# Revit family: KS ALU-PU 80, DS 20, M10-M12, Ø168,3 mit Blechz.
name_source: partatom
category: HLS-Bauteile
revit_build: Autodesk Revit 2018 (Build: 20190510_1515(x64)
units: mm (PartAtom-declared; Revit-internal decimal feet)

## family parameters
Arbeitsebenenbasiert = Ja
Beim Laden mit Abzugskörper schneiden = Nein
Bemaßung runder Anschluss = Durchmesser verwenden
Gemeinsam genutzt = Ja
Immer vertikal = Nein
Raumberechnungspunkt = Nein
Teiletyp = Normal

## types (1)
- Kälteschelle ALU-PU 80, DS 20, M10/M12, Ø168,3
    A = 46 mm  [stored 0.150919 ft]
    AB = 1 mm  [stored 0.00328084 ft]
    Anschluss = M10/M12
    Anschlußhöhe = 47 mm
    Artikelnummer = 75616844/B
    B = 288 mm  [stored 0.944882 ft]
    Baustoffklasse = B2
    Breite = 287 mm  [stored 0.941601 ft]
    D = 168 mm
    D0 = 208 mm
    DF1 = 34 mm
    DF2 = 34 mm
    DS = 20 mm  [stored 0.0656168 ft]
    DVS = 18 mm  [stored 0.0590551 ft]
    Dichte Kern = 80 kg/m³
    Dichte Mantel = 2700 kg/m³
    Dicke Mantel = 0.08 mm
    Dmax = 172 mm  [stored 0.564304 ft]
    Dmin = 167 mm  [stored 0.5479 ft]
    Druckverteilung = Bechzylinder
    Dämmkörper = ALU/PU
    Dämmstärke = 20 mm  [stored 0.0656168 ft]
    EAN = 4250928443793
    Fabrikat = MEFA
    Firma = MEFA Befestigungs- und Montagesysteme GmbH
    Gewicht = 1.41 kg
    Gewicht pro Bauteil = 1.41 kg
    H = 238 mm
    HGA = 22 mm  [stored 0.0721785 ft]
    Kurztext1 = Kälteschelle RG80 ALU/PU
    Kurztext2 = 168,3 mm Iso 20 x 100 mm M10/M12
    L = 100 mm  [stored 0.328084 ft]
    MB = 35 mm  [stored 0.114829 ft]
    MD = 4 mm  [stored 0.0131234 ft]
    Material = Stahl
    Material Mantel = Alufolie
    Materialname = S235
    Mengeneinheit = St
    Oberflaeche = galvanisch verzinkt
    R = 104 mm
    RM = 108 mm
    Rohraußendurchmesser Stahl = 168,3 mm
    Rohrschellentyp = Maxima PSM
    S = 254 mm  [stored 0.833333 ft]
    Schalenlänge = 100 mm
    Vorgabe-Ansicht = 1219 mm
    Wasserdampfdiffusionswiderstand = 18750 µ
    Wärmeleitfähigkeit = 0.025 W/mK
    max. Temperaturbeständigkeit = 120 °C
    max. zul. Last = 2.50 kN
    mittl. Nenndruckfestigkeit Kern = 0,5 N/mm²
    stat. Belastung Kern = 0.10 N/mm²
    vpe = 1

note: [stored X ft] marks values corroborated as IEEE doubles in the binary element streams (Revit-internal decimal feet)

## geometry (parser evidence)
native form markers: Sweep x2
no freeform markers — native parametric forms only
